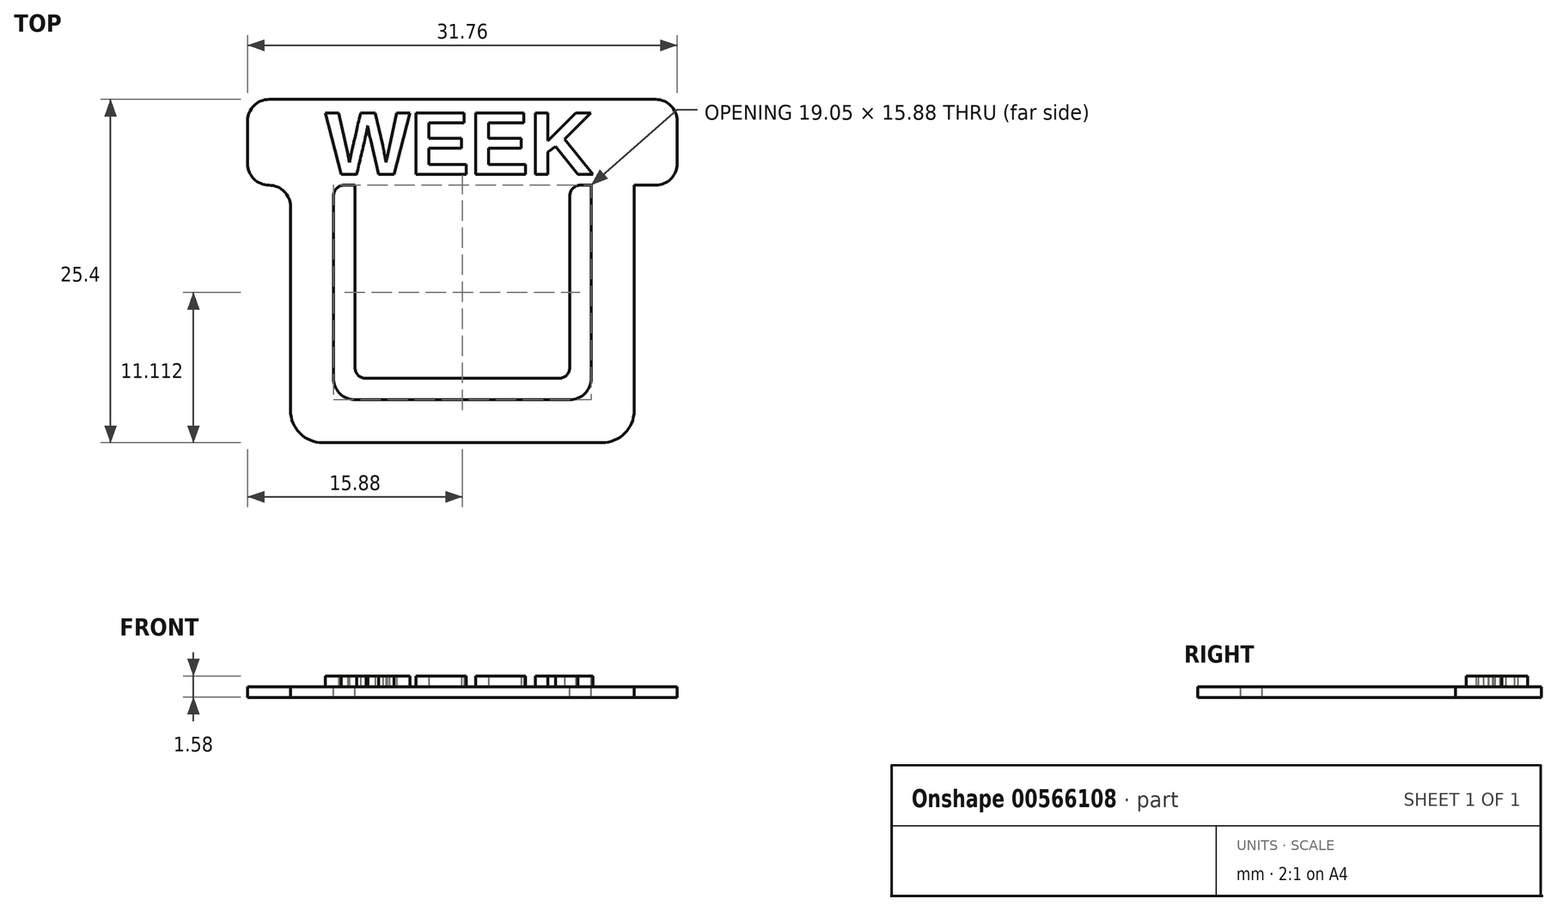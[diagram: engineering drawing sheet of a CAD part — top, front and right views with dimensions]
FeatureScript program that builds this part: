
annotation { "Feature Type Name" : "Feature", "Feature Type Description" : "" }
export const myFeature = defineFeature(function(context is Context, id is Id, definition is map)
    precondition{}
    {
        {
            var Q0;
            Q0=qCreatedBy(makeId("Front.planeOp"),FACE);
            var sketch = newSketch(context, id + "F0", { "sketchPlane" : qUnion([Q0])});
            skLineSegment(sketch, "E0.bottom", {"start": v(12.7, 9.53) * mm, "end": v(-12.7, 9.53) * mm});
            skLineSegment(sketch, "E0.top", {"start": v(12.7, -9.53) * mm, "end": v(-12.7, -9.53) * mm});
            skLineSegment(sketch, "E0.left", {"start": v(12.7, 9.53) * mm, "end": v(12.7, -9.53) * mm});
            skLineSegment(sketch, "E0.right", {"start": v(-12.7, 9.53) * mm, "end": v(-12.7, -9.53) * mm});
            skPoint(sketch, "E0.middle", {"position": v(0, 0) * mm});
            skSolve(sketch);
        }
        {
            var Q0;
            Q0=makeQuery(id+"F0.imprint","IMPRINT",FACE,{"disambiguationData":[TD([[makeQuery(id+"F0.imprint","IMPRINT",EDGE,{"derivedFrom":sQuery(id+"F0.wireOp",EDGE,"E0.bottom")}),1.0]])]});
            extrude(context, id + "F1", {"entities" : qUnion([Q0]), "depth" : 0.8 * mm, "offsetDistance" : 25.4 * mm});
        }
        {
            var Q0;
            Q0=makeQuery(id+"F1.opExtrude","SWEPT_EDGE",EDGE,{"disambiguationData":[OSD([sQuery(id+"F0.wireOp",EDGE,"E0.top"),sQuery(id+"F0.wireOp",EDGE,"E0.left")])]});
            var Q1;
            Q1=makeQuery(id+"F1.opExtrude","SWEPT_EDGE",EDGE,{"disambiguationData":[OSD([sQuery(id+"F0.wireOp",EDGE,"E0.top"),sQuery(id+"F0.wireOp",EDGE,"E0.right")])]});
            fillet(context, id + "F2", {"entities" : qUnion([Q0, Q1]), "radius" : 2.38 * mm, "tangentPropagation" : true, "allowEdgeOverflow" : false});
        }
        {
            var Q0;
            Q0=makeQuery(id+"F1.opExtrude","CAP_FACE",FACE,{"disambiguationData":[OSD([sQuery(id+"F0.wireOp",EDGE,"E0.bottom"),sQuery(id+"F0.wireOp",EDGE,"E0.top"),sQuery(id+"F0.wireOp",EDGE,"E0.left"),sQuery(id+"F0.wireOp",EDGE,"E0.right")])],"isStart":false});
            var sketch = newSketch(context, id + "F3", { "sketchPlane" : qUnion([Q0])});
            skLineSegment(sketch, "E1.bottom", {"start": v(9.52, 9.53) * mm, "end": v(-9.53, 9.53) * mm});
            skLineSegment(sketch, "E1.top", {"start": v(9.53, -6.35) * mm, "end": v(-9.53, -6.35) * mm});
            skLineSegment(sketch, "E1.left", {"start": v(9.52, 9.53) * mm, "end": v(9.53, -6.35) * mm});
            skLineSegment(sketch, "E1.right", {"start": v(-9.53, 9.53) * mm, "end": v(-9.52, -6.35) * mm});
            skPoint(sketch, "E1.middle", {"position": v(0, 0) * mm});
            skSolve(sketch);
        }
        {
            var Q0;
            Q0=makeQuery(id+"F3.imprint","IMPRINT",FACE,{"disambiguationData":[TD([[makeQuery(id+"F3.imprint","IMPRINT",EDGE,{"derivedFrom":sQuery(id+"F3.wireOp",EDGE,"E1.bottom")}),1.0]])]});
            extrude(context, id + "F4", {"entities" : qUnion([Q0]), "operationType" : NewBodyOperationType.REMOVE, "oppositeDirection" : true, "depth" : 4.93 * mm, "offsetDistance" : 25.4 * mm});
        }
        {
            var Q0;
            Q0=makeQuery(id+"F1.opExtrude","CAP_FACE",FACE,{"disambiguationData":[OSD([sQuery(id+"F0.wireOp",EDGE,"E0.bottom"),sQuery(id+"F0.wireOp",EDGE,"E0.top"),sQuery(id+"F0.wireOp",EDGE,"E0.left"),sQuery(id+"F0.wireOp",EDGE,"E0.right")])],"isStart":false});
            var sketch = newSketch(context, id + "F5", { "sketchPlane" : qUnion([Q0])});
            skLineSegment(sketch, "E2.bottom", {"start": v(-15.88, 9.53) * mm, "end": v(15.87, 9.53) * mm});
            skLineSegment(sketch, "E2.top", {"start": v(-15.88, 15.88) * mm, "end": v(15.87, 15.88) * mm});
            skLineSegment(sketch, "E2.left", {"start": v(-15.88, 9.53) * mm, "end": v(-15.88, 15.88) * mm});
            skLineSegment(sketch, "E2.right", {"start": v(15.87, 9.53) * mm, "end": v(15.87, 15.88) * mm});
            skSolve(sketch);
        }
        {
            var Q0;
            Q0=makeQuery(id+"F5.imprint","IMPRINT",FACE,{"disambiguationData":[TD([[makeQuery(id+"F5.imprint","IMPRINT",EDGE,{"derivedFrom":sQuery(id+"F5.wireOp",EDGE,"E2.top")}),-1.0]])]});
            extrude(context, id + "F6", {"entities" : qUnion([Q0]), "operationType" : NewBodyOperationType.ADD, "oppositeDirection" : true, "depth" : 0.8 * mm, "offsetDistance" : 25.4 * mm});
        }
        {
            var Q0;
            Q0=makeQuery(id+"F6.opExtrude","SWEPT_EDGE",EDGE,{"disambiguationData":[OSD([sQuery(id+"F5.wireOp",EDGE,"E2.top"),sQuery(id+"F5.wireOp",EDGE,"E2.left")])]});
            var Q1;
            Q1=makeQuery(id+"F6.opExtrude","SWEPT_EDGE",EDGE,{"disambiguationData":[OSD([sQuery(id+"F5.wireOp",EDGE,"E2.top"),sQuery(id+"F5.wireOp",EDGE,"E2.right")])]});
            var Q2;
            Q2=makeQuery(id+"F6.opExtrude","SWEPT_EDGE",EDGE,{"disambiguationData":[OSD([sQuery(id+"F5.wireOp",EDGE,"E2.bottom"),sQuery(id+"F5.wireOp",EDGE,"E2.right")])]});
            var Q3;
            Q3=makeQuery(id+"F1.opExtrude","SWEPT_EDGE",EDGE,{"disambiguationData":[OSD([sQuery(id+"F0.wireOp",EDGE,"E0.bottom"),sQuery(id+"F0.wireOp",EDGE,"E0.left")])]});
            var Q4;
            Q4=makeQuery(id+"F6.opExtrude","SWEPT_EDGE",EDGE,{"disambiguationData":[OSD([sQuery(id+"F5.wireOp",EDGE,"E2.bottom"),sQuery(id+"F5.wireOp",EDGE,"E2.left")])]});
            var Q5;
            Q5=makeQuery(id+"F1.opExtrude","SWEPT_EDGE",EDGE,{"disambiguationData":[OSD([sQuery(id+"F0.wireOp",EDGE,"E0.bottom"),sQuery(id+"F0.wireOp",EDGE,"E0.right")])]});
            fillet(context, id + "F7", {"entities" : qUnion([Q0, Q1, Q2, Q3, Q4, Q5]), "radius" : 1.59 * mm, "tangentPropagation" : true, "allowEdgeOverflow" : false});
        }
        {
            var Q0;
            Q0=makeQuery(id+"F4.boolean.opBoolean","COPY",EDGE,{"derivedFrom":makeQuery(id+"F4.opExtrude","SWEPT_EDGE",EDGE,{"disambiguationData":[OSD([sQuery(id+"F3.wireOp",EDGE,"E1.top"),sQuery(id+"F3.wireOp",EDGE,"E1.right")])]})});
            var Q1;
            Q1=makeQuery(id+"F4.boolean.opBoolean","COPY",EDGE,{"derivedFrom":makeQuery(id+"F4.opExtrude","SWEPT_EDGE",EDGE,{"disambiguationData":[OSD([sQuery(id+"F3.wireOp",EDGE,"E1.top"),sQuery(id+"F3.wireOp",EDGE,"E1.left")])]})});
            fillet(context, id + "F8", {"entities" : qUnion([Q0, Q1]), "radius" : 1.59 * mm, "tangentPropagation" : true, "allowEdgeOverflow" : false});
        }
        {
            var Q0;
            Q0=makeQuery(id+"F6.boolean.opBoolean","MERGE",FACE,{"derivedFrom":[makeQuery(id+"F1.opExtrude","CAP_FACE",FACE,{"disambiguationData":[OSD([sQuery(id+"F0.wireOp",EDGE,"E0.bottom"),sQuery(id+"F0.wireOp",EDGE,"E0.top"),sQuery(id+"F0.wireOp",EDGE,"E0.left"),sQuery(id+"F0.wireOp",EDGE,"E0.right")])],"isStart":false}),makeQuery(id+"F6.opExtrude","CAP_FACE",FACE,{"disambiguationData":[OSD([sQuery(id+"F5.wireOp",EDGE,"E2.bottom"),sQuery(id+"F5.wireOp",EDGE,"E2.top"),sQuery(id+"F5.wireOp",EDGE,"E2.left"),sQuery(id+"F5.wireOp",EDGE,"E2.right")])],"isStart":true})]});
            var sketch = newSketch(context, id + "F9", { "sketchPlane" : qUnion([Q0])});
            skLineSegment(sketch, "E3.bottom", {"start": v(-7.94, 9.53) * mm, "end": v(7.94, 9.53) * mm});
            skLineSegment(sketch, "E3.top", {"start": v(-7.94, -4.76) * mm, "end": v(7.94, -4.76) * mm});
            skLineSegment(sketch, "E3.left", {"start": v(-7.94, 9.53) * mm, "end": v(-7.94, -4.76) * mm});
            skLineSegment(sketch, "E3.right", {"start": v(7.94, 9.53) * mm, "end": v(7.94, -4.76) * mm});
            skSolve(sketch);
        }
        {
            var Q0;
            Q0=makeQuery(id+"F9.imprint","IMPRINT",FACE,{"disambiguationData":[TD([[makeQuery(id+"F9.imprint","IMPRINT",EDGE,{"derivedFrom":sQuery(id+"F9.wireOp",EDGE,"E3.bottom")}),1.0]])]});
            extrude(context, id + "F10", {"entities" : qUnion([Q0]), "operationType" : NewBodyOperationType.ADD, "oppositeDirection" : true, "depth" : 0.8 * mm, "offsetDistance" : 25.4 * mm});
        }
        {
            var Q0;
            Q0=makeQuery(id+"F10.boolean.opBoolean","MERGE",FACE,{"derivedFrom":[makeQuery(id+"F6.boolean.opBoolean","MERGE",FACE,{"derivedFrom":[makeQuery(id+"F1.opExtrude","CAP_FACE",FACE,{"disambiguationData":[OSD([sQuery(id+"F0.wireOp",EDGE,"E0.bottom"),sQuery(id+"F0.wireOp",EDGE,"E0.top"),sQuery(id+"F0.wireOp",EDGE,"E0.left"),sQuery(id+"F0.wireOp",EDGE,"E0.right")])],"isStart":false}),makeQuery(id+"F6.opExtrude","CAP_FACE",FACE,{"disambiguationData":[OSD([sQuery(id+"F5.wireOp",EDGE,"E2.bottom"),sQuery(id+"F5.wireOp",EDGE,"E2.top"),sQuery(id+"F5.wireOp",EDGE,"E2.left"),sQuery(id+"F5.wireOp",EDGE,"E2.right")])],"isStart":true})]}),makeQuery(id+"F10.opExtrude","CAP_FACE",FACE,{"disambiguationData":[OSD([sQuery(id+"F9.wireOp",EDGE,"E3.bottom"),sQuery(id+"F9.wireOp",EDGE,"E3.top"),sQuery(id+"F9.wireOp",EDGE,"E3.left"),sQuery(id+"F9.wireOp",EDGE,"E3.right")])],"isStart":true})]});
            var sketch = newSketch(context, id + "F11", { "sketchPlane" : qUnion([Q0])});
            skText(sketch, "E4", { "text": "WEEK", "fontName": "Arimo-Bold.ttf"});
            const initialGuessF11  = {"E4": [-0.01012, 0.01032, 1, 0, 0.00476]};
            skSetInitialGuess(sketch, initialGuessF11);
            skSolve(sketch);
        }
        {
            var Q0;
            Q0=makeQuery(id+"F11.imprint","IMPRINT",FACE,{"disambiguationData":[TD([[makeQuery(id+"F11.imprint","IMPRINT",EDGE,{"derivedFrom":sQuery(id+"F11.wireOp",EDGE,"E4.sketch_text.stroke-0")}),-1.0]])]});
            var Q1;
            Q1=makeQuery(id+"F11.imprint","IMPRINT",FACE,{"disambiguationData":[TD([[makeQuery(id+"F11.imprint","IMPRINT",EDGE,{"derivedFrom":sQuery(id+"F11.wireOp",EDGE,"E4.sketch_text.stroke-8")}),-1.0]])]});
            var Q2;
            Q2=makeQuery(id+"F11.imprint","IMPRINT",FACE,{"disambiguationData":[TD([[makeQuery(id+"F11.imprint","IMPRINT",EDGE,{"derivedFrom":sQuery(id+"F11.wireOp",EDGE,"E4.sketch_text.stroke-25")}),-1.0]])]});
            var Q3;
            Q3=makeQuery(id+"F11.imprint","IMPRINT",FACE,{"disambiguationData":[TD([[makeQuery(id+"F11.imprint","IMPRINT",EDGE,{"derivedFrom":sQuery(id+"F11.wireOp",EDGE,"E4.sketch_text.stroke-40")}),-1.0]])]});
            var Q4;
            Q4=makeQuery(id+"F11.imprint","IMPRINT",FACE,{"disambiguationData":[TD([[makeQuery(id+"F11.imprint","IMPRINT",EDGE,{"derivedFrom":sQuery(id+"F11.wireOp",EDGE,"E4.sketch_text.stroke-55")}),-1.0]])]});
            extrude(context, id + "F12", {"entities" : qUnion([Q0, Q1, Q2, Q3, Q4]), "operationType" : NewBodyOperationType.ADD, "depth" : 0.8 * mm, "offsetDistance" : 25.4 * mm});
        }
        {
            var Q0;
            Q0=makeQuery(id+"F10.opExtrude","SWEPT_EDGE",EDGE,{"disambiguationData":[OSD([sQuery(id+"F5.wireOp",EDGE,"E2.bottom"),sQuery(id+"F9.wireOp",EDGE,"E3.bottom"),sQuery(id+"F9.wireOp",EDGE,"E3.left")])]});
            var Q1;
            Q1=makeQuery(id+"F4.boolean.opBoolean","COPY",EDGE,{"derivedFrom":makeQuery(id+"F4.opExtrude","SWEPT_EDGE",EDGE,{"disambiguationData":[OSD([sQuery(id+"F0.wireOp",EDGE,"E0.bottom"),sQuery(id+"F3.wireOp",EDGE,"E1.bottom"),sQuery(id+"F3.wireOp",EDGE,"E1.right")])]})});
            var Q2;
            Q2=makeQuery(id+"F10.opExtrude","SWEPT_EDGE",EDGE,{"disambiguationData":[OSD([sQuery(id+"F5.wireOp",EDGE,"E2.bottom"),sQuery(id+"F9.wireOp",EDGE,"E3.bottom"),sQuery(id+"F9.wireOp",EDGE,"E3.right")])]});
            var Q3;
            Q3=makeQuery(id+"F4.boolean.opBoolean","COPY",EDGE,{"derivedFrom":makeQuery(id+"F4.opExtrude","SWEPT_EDGE",EDGE,{"disambiguationData":[OSD([sQuery(id+"F0.wireOp",EDGE,"E0.bottom"),sQuery(id+"F3.wireOp",EDGE,"E1.bottom"),sQuery(id+"F3.wireOp",EDGE,"E1.left")])]})});
            fillet(context, id + "F13", {"entities" : qUnion([Q0, Q1, Q2, Q3]), "radius" : 0.8 * mm, "tangentPropagation" : true, "allowEdgeOverflow" : false});
        }
        {
            var Q0;
            Q0=makeQuery(id+"F10.opExtrude","SWEPT_EDGE",EDGE,{"disambiguationData":[OSD([sQuery(id+"F9.wireOp",EDGE,"E3.top"),sQuery(id+"F9.wireOp",EDGE,"E3.left")])]});
            var Q1;
            Q1=makeQuery(id+"F10.opExtrude","SWEPT_EDGE",EDGE,{"disambiguationData":[OSD([sQuery(id+"F9.wireOp",EDGE,"E3.top"),sQuery(id+"F9.wireOp",EDGE,"E3.right")])]});
            fillet(context, id + "F14", {"entities" : qUnion([Q0, Q1]), "radius" : 0.8 * mm, "tangentPropagation" : true, "allowEdgeOverflow" : false});
        }
        {
            var Q0;
            Q0=makeQuery(id+"F1.opExtrude","SWEPT_BODY",BODY,{"disambiguationData":[OSD([sQuery(id+"F0.wireOp",EDGE,"E0.bottom"),sQuery(id+"F0.wireOp",EDGE,"E0.top"),sQuery(id+"F0.wireOp",EDGE,"E0.left"),sQuery(id+"F0.wireOp",EDGE,"E0.right")])]});
            var Q1;
            Q1=makeQuery(id+"F6.opExtrude","CAP_EDGE",EDGE,{"disambiguationData":[OSD([sQuery(id+"F5.wireOp",EDGE,"E2.top")])],"isStart":false});
            transform(context, id + "F15", {"entities" : qUnion([Q0]), "transformType" : TransformType.ROTATION, "transformAxis" : qUnion([Q1]), "angle" : 270 * degree, "makeCopy" : false});
        }
    });
